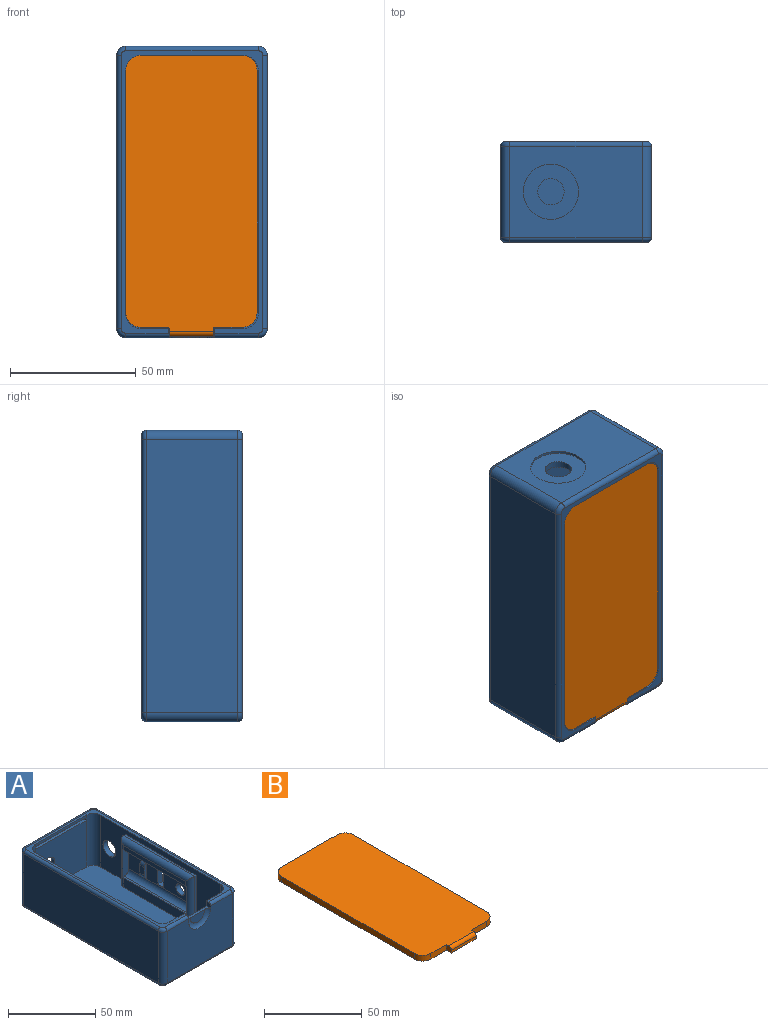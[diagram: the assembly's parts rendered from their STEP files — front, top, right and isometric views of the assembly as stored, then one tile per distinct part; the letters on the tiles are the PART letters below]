
ASSEMBLY  parts=2 mates=1
PART A: 87 faces, bbox 60.6x118.1x40 mm
  f0: plane 50.3x6.65mm, normal (-1,0,0), area 334.5mm2, adj f13,f71,f81,f83
  f1: plane 51.5x12.3mm, normal (-1,0,0), area 492.8mm2, adj f58,f59,f60,f61,f62,f63,f64,f65
  f2: plane 96.81x36.4mm, normal (-1,0,0), area 1551.1mm2, adj f6,f13,f20,f21,f23,f74,f75,f76
  f3: plane 96.81x36.4mm, normal (1,0,0), area 3385.9mm2, adj f6,f13,f18,f19,f53,f55,f56,f57
  f4: plane 52.8x36.4mm, normal (0,1,0), area 1541.8mm2, adj f14,f15,f36,f46,f49
  f5: plane 40.8x1.7mm, normal (0,-1,0), area 69.4mm2, adj f6,f19,f20,f30
  f6: plane 112.4x56.4mm, normal (0,0,1), area 590.4mm2, adj f2,f3,f5,f7,f18,f19,f20,f21
  f7: plane 40.8x36.4mm, normal (0,1,0), area 1420.5mm2, adj f6,f13,f18,f21,f24,f25,f26
  f8: plane 52.8x36.4mm, normal (0,-1,0), area 1762.3mm2, adj f16,f17,f24,f26,f32,f40,f43,f86
  f9: plane 40.8x32.7mm, normal (0,-1,0), area 1247.7mm2, adj f13,f19,f20,f22,f28
  f10: plane 108.8x36.4mm, normal (1,0,0), area 3786.3mm2, adj f14,f17,f23,f34,f47,f58,f59,f60
  f11: plane 108.8x36.4mm, normal (-1,0,0), area 3960.3mm2, adj f15,f16,f38,f42
  f12: plane 112.4x56.4mm, normal (0,0,-1), area 6336.6mm2, adj f41,f42,f43,f44,f45,f46,f47,f48
  f13: plane 108.8x52.8mm, normal (0,0,1), area 5431.8mm2, adj f0,f2,f3,f7,f9,f18,f19,f20
  f14: cylinder r=3.6mm len=36.4mm, axis (0,0,-1), area 205.8mm2, adj f4,f10,f35,f48
  f15: cylinder r=3.6mm len=36.4mm, axis (0,0,1), area 205.8mm2, adj f4,f11,f37,f44
  f16: cylinder r=3.6mm len=36.4mm, axis (0,0,-1), area 205.8mm2, adj f8,f11,f39,f41
  f17: cylinder r=3.6mm len=36.4mm, axis (0,0,1), area 205.8mm2, adj f8,f10,f33,f45
  f18: cylinder r=6mm len=36.4mm, axis (0,0,1), area 342.9mm2, adj f3,f6,f7,f13
  f19: cylinder r=6mm len=36.4mm, axis (0,0,-1), area 342.9mm2, adj f3,f5,f6,f9,f13,f27
  f20: cylinder r=6mm len=36.4mm, axis (0,0,1), area 342.9mm2, adj f2,f5,f6,f9,f13,f29
  f21: cylinder r=6mm len=36.4mm, axis (0,0,-1), area 342.9mm2, adj f2,f6,f7,f13
  f22: cylinder r=5.25mm len=10.5mm, axis (0,1,0), area 85.8mm2, adj f9,f50
  f23: cylinder r=5.25mm len=10.5mm, axis (1,0,0), area 118.8mm2, adj f2,f10
  f24: plane 3.6x3.6mm, normal (1,0,0), area 12.3mm2, adj f6,f7,f8,f25,f40
  f25: plane 18x3.6mm, normal (0,0,1), area 35.7mm2, adj f7,f24,f26,f52,f86
  f26: plane 3.6x3.6mm, normal (-1,0,0), area 12.3mm2, adj f6,f7,f8,f25,f32
  f27: plane 2.1x2mm, normal (1,0,0), area 4.1mm2, adj f19,f28,f30,f31,f51
  f28: plane 40.8x2.1mm, normal (0,0,1), area 85.7mm2, adj f9,f27,f29,f31
  f29: plane 2.1x2mm, normal (-1,0,0), area 4.1mm2, adj f20,f28,f30,f31,f51
  f30: plane 40.8x1.6mm, normal (0,0,-1), area 65.3mm2, adj f5,f27,f29,f51
  f31: plane 40.8x1.5mm, normal (0,-1,0), area 61.2mm2, adj f27,f28,f29,f51
  f32: cylinder r=1.8mm len=17.4mm, axis (-1,0,0), area 49.2mm2, adj f6,f8,f26,f33
  f33: torus R=1.8mm, axis (0,0,1), area 13.1mm2, adj f6,f17,f32,f34
  f34: cylinder r=1.8mm len=108.8mm, axis (0,-1,0), area 307.6mm2, adj f6,f10,f33,f35
  f35: torus R=1.8mm, axis (0,0,1), area 13.1mm2, adj f6,f14,f34,f36
  f36: cylinder r=1.8mm len=52.8mm, axis (1,0,0), area 149.3mm2, adj f4,f6,f35,f37
  f37: torus R=1.8mm, axis (0,0,1), area 13.1mm2, adj f6,f15,f36,f38
  f38: cylinder r=1.8mm len=108.8mm, axis (0,1,0), area 307.6mm2, adj f6,f11,f37,f39
  f39: torus R=1.8mm, axis (0,0,1), area 13.1mm2, adj f6,f16,f38,f40
  f40: cylinder r=1.8mm len=17.4mm, axis (-1,0,0), area 49.2mm2, adj f6,f8,f24,f39
  f41: torus R=1.8mm, axis (0,0,1), area 13.1mm2, adj f12,f16,f42,f43
  f42: cylinder r=1.8mm len=108.8mm, axis (0,-1,0), area 307.6mm2, adj f11,f12,f41,f44
  f43: cylinder r=1.8mm len=52.8mm, axis (1,0,0), area 149.3mm2, adj f8,f12,f41,f45
  f44: torus R=1.8mm, axis (0,0,1), area 13.1mm2, adj f12,f15,f42,f46
  f45: torus R=1.8mm, axis (0,0,1), area 13.1mm2, adj f12,f17,f43,f47
  f46: cylinder r=1.8mm len=52.8mm, axis (-1,0,0), area 149.3mm2, adj f4,f12,f44,f48
  f47: cylinder r=1.8mm len=108.8mm, axis (0,1,0), area 307.6mm2, adj f10,f12,f45,f48
  f48: torus R=1.8mm, axis (0,0,1), area 13.1mm2, adj f12,f14,f46,f47
  f49: cylinder r=11mm len=22mm, axis (0,1,0), area 69.1mm2, adj f4,f50
  f50: plane 22x22mm, normal (0,1,0), area 293.5mm2, adj f22,f49
  f51: cylinder r=0.5mm len=40.8mm, axis (-1,0,0), area 32mm2, adj f27,f29,f30,f31
  f52: plane 11.76x5.88mm, normal (0,-1,0), area 54.4mm2, adj f25,f86
  f53: plane 38.28x1.8mm, normal (0,0,1), area 65.7mm2, adj f3,f54,f55,f57
  f54: plane 34.68x1.8mm, normal (1,0,0), area 62.4mm2, adj f53,f55,f56,f57
  f55: plane 3.6x1.8mm, normal (0.71,-0.71,0), area 6.9mm2, adj f3,f53,f54,f56
  f56: plane 38.28x1.8mm, normal (0.71,0,-0.71), area 92.9mm2, adj f3,f54,f55,f57
  f57: plane 3.6x1.8mm, normal (0.71,0.71,0), area 6.9mm2, adj f3,f53,f54,f56
  f58: plane 10.5x3.6mm, normal (0,1,0), area 37.8mm2, adj f1,f10,f59,f61
  f59: plane 4.5x3.6mm, normal (0,0,-1), area 16.2mm2, adj f1,f10,f58,f60
  f60: plane 10.5x3.6mm, normal (0,-1,0), area 37.8mm2, adj f1,f10,f59,f61
  f61: plane 4.5x3.6mm, normal (0,0,1), area 16.2mm2, adj f1,f10,f58,f60
  f62: cylinder r=3.58mm len=7.15mm, axis (-1,0,0), area 80.9mm2, adj f1,f10
  f63: plane 5x1.8mm, normal (0,1,0), area 9mm2, adj f1,f64,f66,f67
  f64: plane 2x1.8mm, normal (0,0,-1), area 3.6mm2, adj f1,f63,f65,f67
  f65: plane 5x1.8mm, normal (0,-1,0), area 9mm2, adj f1,f64,f66,f67
  f66: plane 2x1.8mm, normal (0,0,1), area 3.6mm2, adj f1,f63,f65,f67
  f67: plane 5x2mm, normal (-1,0,0), area 10mm2, adj f63,f64,f65,f66
  f68: plane 12x2mm, normal (0,-1,0), area 20.3mm2, adj f1,f70,f84,f85
  f69: plane 12x2mm, normal (0,1,0), area 20.3mm2, adj f1,f70,f84,f85
  f70: plane 5.55x3.6mm, normal (-1,0,0), area 20mm2, adj f68,f69,f84,f85
  f71: plane 51.5x1.4mm, normal (0,0,1), area 72.1mm2, adj f0,f72,f77,f80,f81,f83
  f72: plane 19.5x4.95mm, normal (0,-1,0), area 91mm2, adj f1,f71,f73,f79,f80,f81
  f73: plane 51.5x1.4mm, normal (0,0,-1), area 72.1mm2, adj f72,f77,f78,f79,f81,f83
  f74: plane 32.8x1.4mm, normal (0,-1,0), area 45.9mm2, adj f2,f13,f75,f83
  f75: plane 57.5x1.4mm, normal (0,0,1), area 80.5mm2, adj f2,f74,f76,f82
  f76: plane 32.8x1.4mm, normal (0,1,0), area 45.9mm2, adj f2,f13,f75,f81
  f77: plane 19.5x4.95mm, normal (0,1,0), area 91mm2, adj f1,f71,f73,f79,f80,f83
  f78: plane 50.3x3.05mm, normal (-1,0,0), area 153.4mm2, adj f73,f81,f82,f83
  f79: cylinder r=3.6mm len=51.5mm, axis (0,-1,0), area 291.2mm2, adj f1,f72,f73,f77
  f80: cylinder r=3.6mm len=51.5mm, axis (0,1,0), area 291.2mm2, adj f1,f71,f72,f77
  f81: cylinder r=3.6mm len=32.8mm, axis (0,0,1), area 166.3mm2, adj f0,f13,f71,f72,f73,f76,f78,f82
  f82: cylinder r=3.6mm len=57.5mm, axis (0,-1,0), area 310.4mm2, adj f75,f78,f81,f83
  f83: cylinder r=3.6mm len=32.8mm, axis (0,0,-1), area 166.3mm2, adj f0,f13,f71,f73,f74,f77,f78,f82
  f84: cylinder r=3.6mm len=3.6mm, axis (0,1,0), area 14.4mm2, adj f1,f68,f69,f70
  f85: cylinder r=3.6mm len=3.6mm, axis (0,1,0), area 14.4mm2, adj f1,f68,f69,f70
  f86: torus R=5.88mm, axis (0,1,0), area 90mm2, adj f8,f25,f52
PART B: 20 faces, bbox 52.3x113.7x3.6 mm
  f0: plane 11.15x3.6mm, normal (0,-1,0), area 40.1mm2, adj f5,f9,f10,f12
  f1: cylinder r=6mm len=6mm, axis (0,0,-1), area 33.9mm2, adj f2,f8,f9,f10,f15
  f2: plane 40.3x1.8mm, normal (0,1,0), area 72.5mm2, adj f1,f3,f9,f14
  f3: cylinder r=6mm len=6mm, axis (0,0,-1), area 33.9mm2, adj f2,f4,f9,f10,f16
  f4: plane 96.31x3.6mm, normal (-1,0,0), area 346.7mm2, adj f3,f5,f9,f10
  f5: cylinder r=6mm len=6mm, axis (0,0,-1), area 33.9mm2, adj f0,f4,f9,f10
  f6: plane 11.15x3.6mm, normal (0,-1,0), area 40.1mm2, adj f7,f9,f10,f11
  f7: cylinder r=6mm len=6mm, axis (0,0,-1), area 33.9mm2, adj f6,f8,f9,f10
  f8: plane 96.31x3.6mm, normal (1,0,0), area 346.7mm2, adj f1,f7,f9,f10
  f9: plane 110x52.3mm, normal (0,0,1), area 5663.8mm2, adj f0,f1,f2,f3,f4,f5,f6,f7
  f10: plane 113.7x52.3mm, normal (0,0,-1), area 5770.6mm2, adj f0,f1,f3,f4,f5,f6,f7,f8
  f11: plane 3.6x3.6mm, normal (1,0,0), area 12.2mm2, adj f6,f9,f10,f13,f18
  f12: plane 3.6x3.6mm, normal (-1,0,0), area 12.2mm2, adj f0,f9,f10,f13,f18
  f13: plane 18x1.7mm, normal (0,-1,0), area 30.6mm2, adj f10,f11,f12,f18
  f14: plane 40.3x1.3mm, normal (0,0,1), area 52.4mm2, adj f2,f15,f16,f19
  f15: plane 1.8x1.8mm, normal (1,0,0), area 3.2mm2, adj f1,f10,f14,f17,f19
  f16: plane 1.8x1.8mm, normal (-1,0,0), area 3.2mm2, adj f3,f10,f14,f17,f19
  f17: plane 40.3x1.3mm, normal (0,1,0), area 52.4mm2, adj f10,f15,f16,f19
  f18: cylinder r=1.9mm len=18mm, axis (-1,0,0), area 53.7mm2, adj f9,f11,f12,f13
  f19: cylinder r=0.5mm len=40.3mm, axis (-1,0,0), area 31.7mm2, adj f14,f15,f16,f17
PLACE A rot(axis=(1,0,0),90deg) t=(-1.61,76.9,38.66)mm
PLACE B rot(axis=(1,0,0),90deg) t=(-1.86,40.5,38.91)mm
MATE fastened B.f10 <-> A.f53  axis (0,1,0) through (-22.01,40.5,93.06)mm
